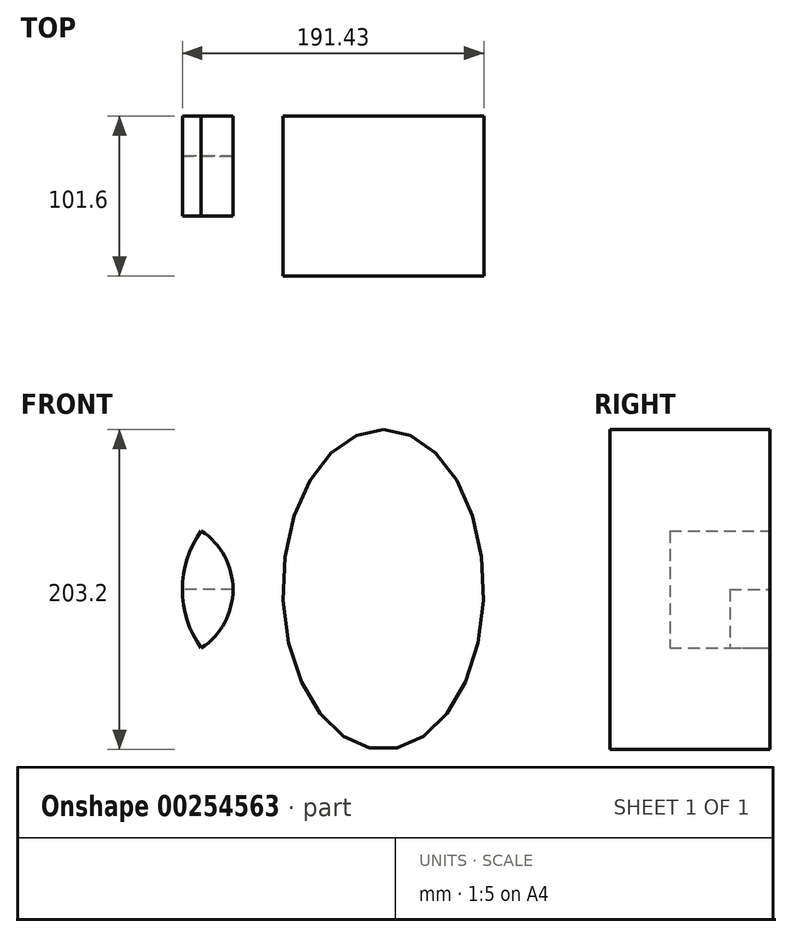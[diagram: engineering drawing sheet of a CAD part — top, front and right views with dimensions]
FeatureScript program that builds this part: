
annotation { "Feature Type Name" : "Feature", "Feature Type Description" : "" }
export const myFeature = defineFeature(function(context is Context, id is Id, definition is map)
    precondition{}
    {
        {
            var Q0;
            Q0=qCreatedBy(makeId("Front.planeOp"),FACE);
            var sketch = newSketch(context, id + "F0", { "sketchPlane" : qUnion([Q0])});
            skLineSegment(sketch, "E0", {"start": v(0, 0) * mm, "end": v(-76.2, 0) * mm});
            skCircle(sketch, "E1", {"center": v(-76.2, 0) * mm, "radius": 44.45 * mm});
            skLineSegment(sketch, "E2", {"start": v(-31.75, 0) * mm, "end": v(-63.5, 0) * mm});
            skPoint(sketch, "E3.second.point", {"position": v(49.2, 0) * mm});
            skPoint(sketch, "E3.second.point.positionSnap0", {"position": v(-47.62, 0) * mm});
            skPoint(sketch, "E3.third.point", {"position": v(46.62, 17.35) * mm});
            skCircle(sketch, "E4", {"center": v(0, 0) * mm, "radius": 63.8 * mm});
            skEllipse(sketch, "E5", {"center": v(63.8, 0) * mm, "majorRadius": 101.6 * mm, "minorRadius": 63.8 * mm, "majorAxis": v(0, 1)});
            skSolve(sketch);
        }
        {
            var Q0;
            {var subQ0=sQuery(id+"F0.wireOp",EDGE,"E4");var subQ1=sQuery(id+"F0.wireOp",EDGE,"E1");var subQ2=makeQuery(id+"F0.imprint","INTERSECT",VERTEX,{"disambiguationData":[OD(0.0)],"derivedFrom":[subQ1,subQ0]});Q0=makeQuery(id+"F0.imprint","IMPRINT",FACE,{"disambiguationData":[TD([[makeQuery(id+"F0.imprint","IMPRINT",EDGE,{"disambiguationData":[TD([[subQ2,-1.0]])],"derivedFrom":subQ1}),1.0]])]});}
            extrude(context, id + "F1", {"entities" : qUnion([Q0]), "depth" : 25.4 * mm});
        }
        {
            var Q0;
            {var subQ3=sQuery(id+"F0.wireOp",EDGE,"E1");var subQ5=sQuery(id+"F0.wireOp",EDGE,"E4");var subQ6=makeQuery(id+"F0.imprint","INTERSECT",VERTEX,{"disambiguationData":[OD(0.0)],"derivedFrom":[subQ3,subQ5]});Q0=makeQuery(id+"F0.imprint","IMPRINT",FACE,{"disambiguationData":[TD([[makeQuery(id+"F0.imprint","IMPRINT",EDGE,{"disambiguationData":[TD([[subQ6,1.0]])],"derivedFrom":subQ5}),1.0]])]});}
            var Q1;
            {var subQ3=sQuery(id+"F0.wireOp",EDGE,"E1");var subQ5=sQuery(id+"F0.wireOp",EDGE,"E4");var subQ6=makeQuery(id+"F0.imprint","INTERSECT",VERTEX,{"disambiguationData":[OD(1.0)],"derivedFrom":[subQ3,subQ5]});Q1=makeQuery(id+"F0.imprint","IMPRINT",FACE,{"disambiguationData":[TD([[makeQuery(id+"F0.imprint","IMPRINT",EDGE,{"disambiguationData":[TD([[subQ6,-1.0]])],"derivedFrom":subQ5}),1.0]])]});}
            var Q2;
            {var subQ0=sQuery(id+"F0.wireOp",EDGE,"E2");Q2=makeQuery(id+"F0.imprint","IMPRINT",FACE,{"disambiguationData":[TD([[makeQuery(id+"F0.imprint","IMPRINT",EDGE,{"derivedFrom":subQ0}),1.0]])]});}
            var Q3;
            {var subQ0=sQuery(id+"F0.wireOp",EDGE,"E2");Q3=makeQuery(id+"F0.imprint","IMPRINT",FACE,{"disambiguationData":[TD([[makeQuery(id+"F0.imprint","IMPRINT",EDGE,{"derivedFrom":subQ0}),-1.0]])]});}
            extrude(context, id + "F2", {"entities" : qUnion([Q0, Q1, Q2, Q3]), "depth" : 63.5 * mm});
        }
        {
            var Q0;
            {var subQ0=sQuery(id+"F0.wireOp",EDGE,"E5");var subQ1=sQuery(id+"F0.wireOp",EDGE,"E4");var subQ2=makeQuery(id+"F0.imprint","INTERSECT",VERTEX,{"disambiguationData":[OD(0.0)],"derivedFrom":[subQ1,subQ0]});Q0=makeQuery(id+"F0.imprint","IMPRINT",FACE,{"disambiguationData":[TD([[makeQuery(id+"F0.imprint","IMPRINT",EDGE,{"disambiguationData":[TD([[subQ2,1.0]])],"derivedFrom":subQ1}),-1.0]])]});}
            var Q1;
            {var subQ0=sQuery(id+"F0.wireOp",EDGE,"E5");var subQ1=sQuery(id+"F0.wireOp",EDGE,"E4");var subQ2=makeQuery(id+"F0.imprint","INTERSECT",VERTEX,{"disambiguationData":[OD(0.0)],"derivedFrom":[subQ1,subQ0]});Q1=makeQuery(id+"F0.imprint","IMPRINT",FACE,{"disambiguationData":[TD([[makeQuery(id+"F0.imprint","IMPRINT",EDGE,{"disambiguationData":[TD([[subQ2,1.0]])],"derivedFrom":subQ1}),1.0]])]});}
            extrude(context, id + "F3", {"entities" : qUnion([Q0, Q1]), "depth" : 101.6 * mm});
        }
    });
